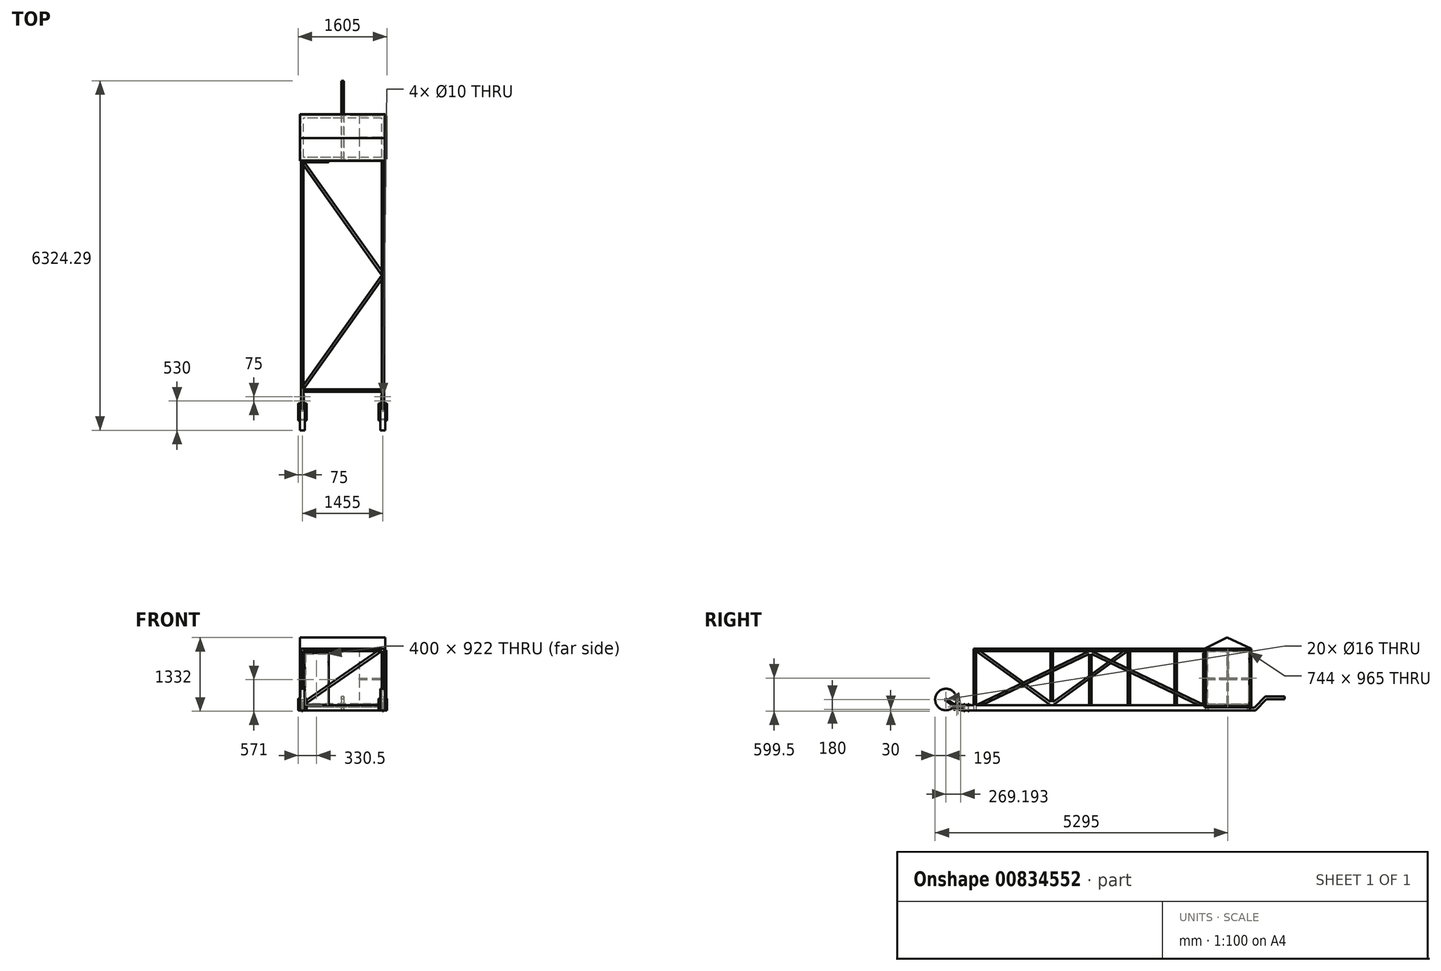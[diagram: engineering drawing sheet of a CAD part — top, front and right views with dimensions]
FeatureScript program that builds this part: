
annotation { "Feature Type Name" : "Feature", "Feature Type Description" : "" }
export const myFeature = defineFeature(function(context is Context, id is Id, definition is map)
    precondition{}
    {
        {
            var Q0;
            Q0=qCreatedBy(makeId("Top.planeOp"),FACE);
            var sketch = newSketch(context, id + "F0", { "sketchPlane" : qUnion([Q0])});
            skLineSegment(sketch, "E0.bottom", {"start": v(750, -2500) * mm, "end": v(-750, -2500) * mm});
            skLineSegment(sketch, "E0.top", {"start": v(750, 2500) * mm, "end": v(-750, 2500) * mm});
            skLineSegment(sketch, "E0.left", {"start": v(750, -2500) * mm, "end": v(750, 2500) * mm});
            skLineSegment(sketch, "E0.right", {"start": v(-750, -2500) * mm, "end": v(-750, 2500) * mm});
            skPoint(sketch, "E0.middle", {"position": v(0, 0) * mm});
            skLineSegment(sketch, "E1.bottom", {"start": v(705, -2455) * mm, "end": v(-705, -2455) * mm});
            skLineSegment(sketch, "E1.top", {"start": v(705, 2455) * mm, "end": v(-705, 2455) * mm});
            skLineSegment(sketch, "E1.left", {"start": v(705, -2455) * mm, "end": v(705, 2455) * mm});
            skLineSegment(sketch, "E1.right", {"start": v(-705, -2455) * mm, "end": v(-705, 2455) * mm});
            skSolve(sketch);
        }
        {
            var Q0;
            Q0 = qSketchRegion(id + "F0", true);
            extrude(context, id + "F1", {"entities" : qUnion([Q0]), "depth" : 95 * mm, "offsetDistance" : 25 * mm});
        }
        {
            var Q0;
            Q0=makeQuery(id+"F1.opExtrude","SWEPT_FACE",FACE,{"disambiguationData":[OSD([sQuery(id+"F0.wireOp",EDGE,"E0.bottom")])]});
            var sketch = newSketch(context, id + "F2", { "sketchPlane" : qUnion([Q0])});
            skLineSegment(sketch, "E2.bottom", {"start": v(750, 95) * mm, "end": v(705, 95) * mm});
            skLineSegment(sketch, "E2.top", {"start": v(750, 0) * mm, "end": v(705, 0) * mm});
            skLineSegment(sketch, "E2.left", {"start": v(750, 95) * mm, "end": v(750, 0) * mm});
            skLineSegment(sketch, "E2.right", {"start": v(705, 95) * mm, "end": v(705, 0) * mm});
            skLineSegment(sketch, "E3.bottom", {"start": v(-750, 95) * mm, "end": v(-705, 95) * mm});
            skLineSegment(sketch, "E3.top", {"start": v(-750, 0) * mm, "end": v(-705, 0) * mm});
            skLineSegment(sketch, "E3.left", {"start": v(-750, 95) * mm, "end": v(-750, 0) * mm});
            skLineSegment(sketch, "E3.right", {"start": v(-705, 95) * mm, "end": v(-705, 0) * mm});
            skSolve(sketch);
        }
        {
            var Q0;
            Q0 = qSketchRegion(id + "F2", true);
            extrude(context, id + "F3", {"entities" : qUnion([Q0]), "operationType" : NewBodyOperationType.ADD, "depth" : 200 * mm, "offsetDistance" : 25 * mm});
        }
        {
            var Q0;
            Q0=makeQuery(id+"F3.opExtrude","SWEPT_FACE",FACE,{"disambiguationData":[OSD([sQuery(id+"F2.wireOp",EDGE,"E2.right")])]});
            var Q1;
            Q1=makeQuery(id+"F3.boolean.opBoolean","MERGE",FACE,{"derivedFrom":[makeQuery(id+"F1.opExtrude","SWEPT_FACE",FACE,{"disambiguationData":[OSD([sQuery(id+"F0.wireOp",EDGE,"E0.left")])]}),makeQuery(id+"F3.opExtrude","SWEPT_FACE",FACE,{"disambiguationData":[OSD([sQuery(id+"F2.wireOp",EDGE,"E2.left")])]})]});
            cPlane(context, id + "F4", {"entities" : qUnion([Q0, Q1]), "cplaneType" : CPlaneType.MID_PLANE, "offset" : 25 * mm, "width" : 150 * mm, "height" : 150 * mm});
        }
        {
            var Q0;
            Q0=qCreatedBy(id+"F4.planeOp",FACE);
            var sketch = newSketch(context, id + "F5", { "sketchPlane" : qUnion([Q0])});
            skCircle(sketch, "E4", {"center": v(3000, 195) * mm, "radius": 195 * mm});
            skLineSegment(sketch, "E5", {"start": v(2248.79, 0) * mm, "end": v(2700, 0) * mm, "construction": true});
            skSolve(sketch);
        }
        {
            var Q0;
            Q0 = qSketchRegion(id + "F5", true);
            extrude(context, id + "F6", {"entities" : qUnion([Q0]), "endBound" : BoundingType.SYMMETRIC, "depth" : 90 * mm, "offsetDistance" : 25 * mm});
        }
        {
            var Q0;
            Q0=makeQuery(id+"F6.opExtrude","CAP_FACE",FACE,{"disambiguationData":[OSD([sQuery(id+"F5.wireOp",EDGE,"E4")])],"isStart":true});
            var sketch = newSketch(context, id + "F7", { "sketchPlane" : qUnion([Q0])});
            skCircle(sketch, "E6", {"center": v(-3000, 195) * mm, "radius": 8 * mm});
            skSolve(sketch);
        }
        {
            var Q0;
            Q0 = qSketchRegion(id + "F7", true);
            extrude(context, id + "F8", {"entities" : qUnion([Q0]), "depth" : 25 * mm, "offsetDistance" : 25 * mm, "hasSecondDirection" : true, "secondDirectionOppositeDirection" : true, "secondDirectionDepth" : (90 + 25) * mm});
        }
        {
            var Q0;
            Q0=makeQuery(id+"F6.opExtrude","CAP_FACE",FACE,{"disambiguationData":[OSD([sQuery(id+"F5.wireOp",EDGE,"E4")])],"isStart":true});
            var sketch = newSketch(context, id + "F9", { "sketchPlane" : qUnion([Q0])});
            skLineSegment(sketch, "E7", {"start": v(-3020.63, 190.75) * mm, "end": v(-2726.68, -5.8) * mm});
            skLineSegment(sketch, "E8", {"start": v(-2726.68, -5.8) * mm, "end": v(-2710, 19.13) * mm});
            skLineSegment(sketch, "E9", {"start": v(-2710, 19.13) * mm, "end": v(-3004.3, 215.93) * mm});
            skLineSegment(sketch, "E10", {"start": v(-3004.3, 215.93) * mm, "end": v(-3020.63, 190.75) * mm});
            skCircle(sketch, "E11.0", {"center": v(-3000, 195) * mm, "radius": 8 * mm});
            skCircle(sketch, "E12", {"center": v(-2730.8, 15) * mm, "radius": 8 * mm});
            skSolve(sketch);
        }
        {
            var Q0;
            Q0 = qSketchRegion(id + "F9", true);
            extrude(context, id + "F10", {"entities" : qUnion([Q0]), "depth" : 30 * mm, "offsetDistance" : 25 * mm});
        }
        {
            var Q0;
            Q0=qCreatedBy(id+"F4.planeOp",FACE);
            var sketch = newSketch(context, id + "F11", { "sketchPlane" : qUnion([Q0])});
            skLineSegment(sketch, "E13.bottom", {"start": v(2700, 95) * mm, "end": v(2555, 95) * mm});
            skLineSegment(sketch, "E13.top", {"start": v(2700, 0) * mm, "end": v(2555, 0) * mm});
            skLineSegment(sketch, "E13.left", {"start": v(2700, 95) * mm, "end": v(2700, 0) * mm});
            skLineSegment(sketch, "E14.bottom", {"start": v(2705, 100) * mm, "end": v(2555, 100) * mm});
            skLineSegment(sketch, "E14.top", {"start": v(2705, -5) * mm, "end": v(2555, -5) * mm});
            skLineSegment(sketch, "E14.left", {"start": v(2705, 100) * mm, "end": v(2705, -5) * mm});
            skLineSegment(sketch, "E14.right", {"start": v(2555, 100) * mm, "end": v(2555, 95) * mm});
            skLineSegment(sketch, "E15.trimOffspring", {"start": v(2555, 0) * mm, "end": v(2555, -5) * mm});
            skSolve(sketch);
        }
        {
            var Q0;
            Q0 = qSketchRegion(id + "F11", true);
            extrude(context, id + "F12", {"entities" : qUnion([Q0]), "endBound" : BoundingType.SYMMETRIC, "oppositeDirection" : true, "depth" : 50 * mm, "offsetDistance" : 25 * mm});
        }
        {
            var Q0;
            Q0=makeQuery(id+"F10.opExtrude","SWEPT_BODY",BODY,{"disambiguationData":[OSD([sQuery(id+"F9.wireOp",EDGE,"E7"),sQuery(id+"F9.wireOp",EDGE,"E8"),sQuery(id+"F9.wireOp",EDGE,"E9"),sQuery(id+"F9.wireOp",EDGE,"E10"),sQuery(id+"F9.wireOp",EDGE,"E11.0"),sQuery(id+"F9.wireOp",EDGE,"E12")])]});
            var Q1;
            Q1=qCreatedBy(id+"F4.planeOp",FACE);
            mirror(context, id + "F13", {"entities" : qUnion([Q0]), "mirrorPlane" : qUnion([Q1])});
        }
        {
            var Q0;
            Q0=makeQuery(id+"F12.opExtrude","CAP_FACE",FACE,{"disambiguationData":[OSD([sQuery(id+"F11.wireOp",EDGE,"E13.bottom"),sQuery(id+"F11.wireOp",EDGE,"E13.top"),sQuery(id+"F11.wireOp",EDGE,"E13.left"),sQuery(id+"F11.wireOp",EDGE,"E14.bottom"),sQuery(id+"F11.wireOp",EDGE,"E14.top"),sQuery(id+"F11.wireOp",EDGE,"E14.left"),sQuery(id+"F11.wireOp",EDGE,"E14.right"),sQuery(id+"F11.wireOp",EDGE,"E15.trimOffspring")])],"isStart":false});
            var sketch = newSketch(context, id + "F14", { "sketchPlane" : qUnion([Q0])});
            skLineSegment(sketch, "E16", {"start": v(-2705, -5) * mm, "end": v(-2735.9, -5) * mm});
            skLineSegment(sketch, "E17", {"start": v(-2802.7, 100) * mm, "end": v(-2705, 100) * mm});
            skLineSegment(sketch, "E18", {"start": v(-2705, 100) * mm, "end": v(-2705, -5) * mm});
            skCircle(sketch, "E19", {"center": v(-2780, 85) * mm, "radius": 8 * mm});
            skLineSegment(sketch, "E20", {"start": v(-2802.7, 100) * mm, "end": v(-2802.7, 78.2) * mm});
            skLineSegment(sketch, "E21", {"start": v(-2802.7, 78.2) * mm, "end": v(-2735.9, -5) * mm});
            skCircle(sketch, "E22.0", {"center": v(-2730.8, 15) * mm, "radius": 8 * mm});
            skSolve(sketch);
        }
        {
            var Q0;
            Q0 = qSketchRegion(id + "F14", true);
            extrude(context, id + "F15", {"entities" : qUnion([Q0]), "oppositeDirection" : true, "depth" : 5 * mm, "offsetDistance" : 25 * mm});
        }
        {
            var Q0;
            Q0=makeQuery(id+"F15.opExtrude","SWEPT_BODY",BODY,{"disambiguationData":[OSD([sQuery(id+"F14.wireOp",EDGE,"E16"),sQuery(id+"F14.wireOp",EDGE,"E17"),sQuery(id+"F14.wireOp",EDGE,"E18"),sQuery(id+"F14.wireOp",EDGE,"E19"),sQuery(id+"F14.wireOp",EDGE,"E20"),sQuery(id+"F14.wireOp",EDGE,"E21"),sQuery(id+"F14.wireOp",EDGE,"E22.0")])]});
            var Q1;
            Q1=qCreatedBy(id+"F4.planeOp",FACE);
            mirror(context, id + "F16", {"entities" : qUnion([Q0]), "mirrorPlane" : qUnion([Q1])});
        }
        {
            var Q0;
            Q0=makeQuery(id+"F10.opExtrude","CAP_FACE",FACE,{"disambiguationData":[OSD([sQuery(id+"F9.wireOp",EDGE,"E7"),sQuery(id+"F9.wireOp",EDGE,"E8"),sQuery(id+"F9.wireOp",EDGE,"E9"),sQuery(id+"F9.wireOp",EDGE,"E10"),sQuery(id+"F9.wireOp",EDGE,"E11.0"),sQuery(id+"F9.wireOp",EDGE,"E12")])],"isStart":false});
            var sketch = newSketch(context, id + "F17", { "sketchPlane" : qUnion([Q0])});
            skCircle(sketch, "E23", {"center": v(-2801.93, 62.56) * mm, "radius": 8 * mm});
            skLineSegment(sketch, "E24", {"start": v(-2146.6, -375.64) * mm, "end": v(-2801.93, 62.56) * mm, "construction": true});
            skLineSegment(sketch, "E25", {"start": v(-2801.93, 62.56) * mm, "end": v(-2730.8, 15) * mm, "construction": true});
            skLineSegment(sketch, "E26", {"start": v(-2730.8, 15) * mm, "end": v(-2780, 85) * mm, "construction": true});
            skCircle(sketch, "E27.0", {"center": v(-2780, 85) * mm, "radius": 8 * mm, "construction": true});
            skSolve(sketch);
        }
        {
            var Q0;
            Q0 = qSketchRegion(id + "F17", true);
            extrude(context, id + "F18", {"entities" : qUnion([Q0]), "operationType" : NewBodyOperationType.REMOVE, "endBound" : BoundingType.THROUGH_ALL, "oppositeDirection" : true, "depth" : 25 * mm, "offsetDistance" : 25 * mm});
        }
        {
            var Q0;
            Q0=makeQuery(id+"F10.opExtrude","CAP_FACE",FACE,{"disambiguationData":[OSD([sQuery(id+"F9.wireOp",EDGE,"E7"),sQuery(id+"F9.wireOp",EDGE,"E8"),sQuery(id+"F9.wireOp",EDGE,"E9"),sQuery(id+"F9.wireOp",EDGE,"E10"),sQuery(id+"F9.wireOp",EDGE,"E11.0"),sQuery(id+"F9.wireOp",EDGE,"E12")])],"isStart":false});
            var sketch = newSketch(context, id + "F19", { "sketchPlane" : qUnion([Q0])});
            skCircle(sketch, "E28.0", {"center": v(-2801.93, 62.56) * mm, "radius": 8 * mm});
            skSolve(sketch);
        }
        {
            var Q0;
            Q0 = qSketchRegion(id + "F19", true);
            var Q1;
            Q1=makeQuery(id+"F13.opPattern","COPY",FACE,{"derivedFrom":makeQuery(id+"F10.opExtrude","CAP_FACE",FACE,{"disambiguationData":[OSD([sQuery(id+"F9.wireOp",EDGE,"E7"),sQuery(id+"F9.wireOp",EDGE,"E8"),sQuery(id+"F9.wireOp",EDGE,"E9"),sQuery(id+"F9.wireOp",EDGE,"E10"),sQuery(id+"F9.wireOp",EDGE,"E11.0"),sQuery(id+"F9.wireOp",EDGE,"E12")])],"isStart":false}),"instanceName":"1"});
            extrude(context, id + "F20", {"entities" : qUnion([Q0]), "endBound" : BoundingType.UP_TO_SURFACE, "oppositeDirection" : true, "depth" : 25 * mm, "endBoundEntityFace" : qUnion([Q1]), "offsetDistance" : 25 * mm});
        }
        {
            var Q0;
            Q0=makeQuery(id+"F16.opPattern","COPY",FACE,{"derivedFrom":makeQuery(id+"F15.opExtrude","CAP_FACE",FACE,{"disambiguationData":[OSD([sQuery(id+"F14.wireOp",EDGE,"E16"),sQuery(id+"F14.wireOp",EDGE,"E17"),sQuery(id+"F14.wireOp",EDGE,"E18"),sQuery(id+"F14.wireOp",EDGE,"E19"),sQuery(id+"F14.wireOp",EDGE,"E20"),sQuery(id+"F14.wireOp",EDGE,"E21"),sQuery(id+"F14.wireOp",EDGE,"E22.0")])],"isStart":true}),"instanceName":"1"});
            var sketch = newSketch(context, id + "F21", { "sketchPlane" : qUnion([Q0])});
            skCircle(sketch, "E29.0", {"center": v(2780, 85) * mm, "radius": 8 * mm});
            skSolve(sketch);
        }
        {
            var Q0;
            Q0 = qSketchRegion(id + "F21", true);
            var Q1;
            Q1=makeQuery(id+"F15.opExtrude","CAP_FACE",FACE,{"disambiguationData":[OSD([sQuery(id+"F14.wireOp",EDGE,"E16"),sQuery(id+"F14.wireOp",EDGE,"E17"),sQuery(id+"F14.wireOp",EDGE,"E18"),sQuery(id+"F14.wireOp",EDGE,"E19"),sQuery(id+"F14.wireOp",EDGE,"E20"),sQuery(id+"F14.wireOp",EDGE,"E21"),sQuery(id+"F14.wireOp",EDGE,"E22.0")])],"isStart":true});
            extrude(context, id + "F22", {"entities" : qUnion([Q0]), "endBound" : BoundingType.UP_TO_SURFACE, "oppositeDirection" : true, "depth" : 25 * mm, "endBoundEntityFace" : qUnion([Q1]), "offsetDistance" : 25 * mm});
        }
        {
            var Q0;
            Q0=makeQuery(id+"F10.opExtrude","CAP_FACE",FACE,{"disambiguationData":[OSD([sQuery(id+"F9.wireOp",EDGE,"E7"),sQuery(id+"F9.wireOp",EDGE,"E8"),sQuery(id+"F9.wireOp",EDGE,"E9"),sQuery(id+"F9.wireOp",EDGE,"E10"),sQuery(id+"F9.wireOp",EDGE,"E11.0"),sQuery(id+"F9.wireOp",EDGE,"E12")])],"isStart":false});
            var sketch = newSketch(context, id + "F23", { "sketchPlane" : qUnion([Q0])});
            skCircle(sketch, "E30.0", {"center": v(-2730.8, 15) * mm, "radius": 8 * mm});
            skSolve(sketch);
        }
        {
            var Q0;
            Q0 = qSketchRegion(id + "F23", true);
            var Q1;
            Q1=makeQuery(id+"F13.opPattern","COPY",FACE,{"derivedFrom":makeQuery(id+"F10.opExtrude","CAP_FACE",FACE,{"disambiguationData":[OSD([sQuery(id+"F9.wireOp",EDGE,"E7"),sQuery(id+"F9.wireOp",EDGE,"E8"),sQuery(id+"F9.wireOp",EDGE,"E9"),sQuery(id+"F9.wireOp",EDGE,"E10"),sQuery(id+"F9.wireOp",EDGE,"E11.0"),sQuery(id+"F9.wireOp",EDGE,"E12")])],"isStart":false}),"instanceName":"1"});
            extrude(context, id + "F24", {"entities" : qUnion([Q0]), "endBound" : BoundingType.UP_TO_SURFACE, "oppositeDirection" : true, "depth" : 25 * mm, "endBoundEntityFace" : qUnion([Q1]), "offsetDistance" : 25 * mm});
        }
        {
            var Q0;
            Q0=makeQuery(id+"F15.opExtrude","SWEPT_EDGE",EDGE,{"disambiguationData":[OSD([sQuery(id+"F14.wireOp",EDGE,"E17"),sQuery(id+"F14.wireOp",EDGE,"E20")])]});
            cPlane(context, id + "F25", {"entities" : qUnion([Q0]), "cplaneType" : CPlaneType.LINE_ANGLE, "offset" : 25 * mm, "angle" : 47 * degree, "width" : 150 * mm, "height" : 150 * mm});
        }
        {
            var Q0;
            Q0=qCreatedBy(id+"F25.planeOp",FACE);
            var sketch = newSketch(context, id + "F26", { "sketchPlane" : qUnion([Q0])});
            skCircle(sketch, "E31", {"center": v(727.5, -2091.13) * mm, "radius": 6 * mm});
            skLineSegment(sketch, "E32", {"start": v(1068.27, -2099.13) * mm, "end": v(887.35, -2099.13) * mm, "construction": true});
            skLineSegment(sketch, "E33", {"start": v(882.86, -2083.13) * mm, "end": v(1061.54, -2083.13) * mm, "construction": true});
            skLineSegment(sketch, "E34", {"start": v(727.5, -2091.13) * mm, "end": v(883.31, -2091.13) * mm, "construction": true});
            skLineSegment(sketch, "E35", {"start": v(727.5, -2091.13) * mm, "end": v(727.5, -2020.53) * mm, "construction": true});
            skSolve(sketch);
        }
        {
            var Q0;
            Q0 = qSketchRegion(id + "F26", true);
            extrude(context, id + "F27", {"entities" : qUnion([Q0]), "depth" : 50 * mm, "offsetDistance" : 25 * mm, "hasSecondDirection" : true, "secondDirectionOppositeDirection" : true, "secondDirectionDepth" : 100 * mm});
        }
        {
            var Q0;
            Q0=makeQuery(id+"F27.opExtrude","CAP_FACE",FACE,{"disambiguationData":[OSD([sQuery(id+"F26.wireOp",EDGE,"E31")])],"isStart":false});
            var sketch = newSketch(context, id + "F28", { "sketchPlane" : qUnion([Q0])});
            skCircle(sketch, "E36.cCircle", {"center": v(727.5, -2091.13) * mm, "radius": 9.5 * mm, "construction": true});
            skLineSegment(sketch, "E36.0", {"start": v(722.02, -2081.63) * mm, "end": v(732.98, -2081.63) * mm});
            skLineSegment(sketch, "E36.1", {"start": v(732.98, -2081.63) * mm, "end": v(738.47, -2091.13) * mm});
            skLineSegment(sketch, "E36.2", {"start": v(738.47, -2091.13) * mm, "end": v(732.98, -2100.63) * mm});
            skLineSegment(sketch, "E36.3", {"start": v(732.98, -2100.63) * mm, "end": v(722.02, -2100.63) * mm});
            skLineSegment(sketch, "E36.4", {"start": v(722.02, -2100.63) * mm, "end": v(716.53, -2091.13) * mm});
            skLineSegment(sketch, "E36.5", {"start": v(716.53, -2091.13) * mm, "end": v(722.02, -2081.63) * mm});
            skPoint(sketch, "E36.0.midPoint", {"position": v(727.5, -2081.63) * mm});
            skSolve(sketch);
        }
        {
            var Q0;
            Q0 = qSketchRegion(id + "F28", true);
            extrude(context, id + "F29", {"entities" : qUnion([Q0]), "operationType" : NewBodyOperationType.ADD, "depth" : 12 * mm, "offsetDistance" : 25 * mm});
        }
        {
            var Q0;
            Q0=makeQuery(id+"F27.opExtrude","SWEPT_BODY",BODY,{"disambiguationData":[OSD([sQuery(id+"F26.wireOp",EDGE,"E31")])]});
            var Q1;
            Q1=makeQuery(id+"F20.opExtrude","SWEPT_BODY",BODY,{"disambiguationData":[OSD([sQuery(id+"F19.wireOp",EDGE,"E28.0")])]});
            var Q2;
            Q2=makeQuery(id+"F22.opExtrude","SWEPT_BODY",BODY,{"disambiguationData":[OSD([sQuery(id+"F21.wireOp",EDGE,"E29.0")])]});
            booleanBodies(context, id + "F30", {"operationType" : BooleanOperationType.SUBTRACTION, "tools" : qUnion([Q0]), "targets" : qUnion([Q1, Q2]), "keepTools" : true});
        }
        {
            var Q0;
            Q0=makeQuery(id+"F12.opExtrude","SWEPT_FACE",FACE,{"disambiguationData":[OSD([sQuery(id+"F11.wireOp",EDGE,"E14.bottom")])]});
            var sketch = newSketch(context, id + "F31", { "sketchPlane" : qUnion([Q0])});
            skCircle(sketch, "E37", {"center": v(727.5, -2665) * mm, "radius": 5 * mm});
            skCircle(sketch, "E38", {"center": v(727.5, -2590) * mm, "radius": 5 * mm});
            skLineSegment(sketch, "E39", {"start": v(727.5, -2665) * mm, "end": v(727.5, -2590) * mm, "construction": true});
            skSolve(sketch);
        }
        {
            var Q0;
            Q0 = qSketchRegion(id + "F31", true);
            extrude(context, id + "F32", {"entities" : qUnion([Q0]), "oppositeDirection" : true, "depth" : 115 * mm, "offsetDistance" : 25 * mm});
        }
        {
            var Q0;
            Q0=makeQuery(id+"F12.opExtrude","SWEPT_FACE",FACE,{"disambiguationData":[OSD([sQuery(id+"F11.wireOp",EDGE,"E14.top")])]});
            var sketch = newSketch(context, id + "F33", { "sketchPlane" : qUnion([Q0])});
            skCircle(sketch, "E40.0", {"center": v(727.5, 2665) * mm, "radius": 5 * mm});
            skCircle(sketch, "E41.0", {"center": v(727.5, 2590) * mm, "radius": 5 * mm});
            skCircle(sketch, "E42.cCircle", {"center": v(727.5, 2665) * mm, "radius": 8.5 * mm, "construction": true});
            skLineSegment(sketch, "E42.0", {"start": v(724.08, 2655.8) * mm, "end": v(717.82, 2663.37) * mm});
            skLineSegment(sketch, "E42.1", {"start": v(717.82, 2663.37) * mm, "end": v(721.25, 2672.56) * mm});
            skLineSegment(sketch, "E42.2", {"start": v(721.25, 2672.56) * mm, "end": v(730.92, 2674.2) * mm});
            skLineSegment(sketch, "E42.3", {"start": v(730.92, 2674.2) * mm, "end": v(737.18, 2666.63) * mm});
            skLineSegment(sketch, "E42.4", {"start": v(737.18, 2666.63) * mm, "end": v(733.75, 2657.44) * mm});
            skLineSegment(sketch, "E42.5", {"start": v(733.75, 2657.44) * mm, "end": v(724.08, 2655.8) * mm});
            skPoint(sketch, "E42.0.midPoint", {"position": v(720.95, 2659.58) * mm});
            skCircle(sketch, "E43.cCircle", {"center": v(727.5, 2590) * mm, "radius": 8.5 * mm, "construction": true});
            skLineSegment(sketch, "E43.0", {"start": v(720.8, 2582.83) * mm, "end": v(717.94, 2592.22) * mm});
            skLineSegment(sketch, "E43.1", {"start": v(717.94, 2592.22) * mm, "end": v(724.65, 2599.4) * mm});
            skLineSegment(sketch, "E43.2", {"start": v(724.65, 2599.4) * mm, "end": v(734.2, 2597.17) * mm});
            skLineSegment(sketch, "E43.3", {"start": v(734.2, 2597.17) * mm, "end": v(737.06, 2587.78) * mm});
            skLineSegment(sketch, "E43.4", {"start": v(737.06, 2587.78) * mm, "end": v(730.35, 2580.6) * mm});
            skLineSegment(sketch, "E43.5", {"start": v(730.35, 2580.6) * mm, "end": v(720.8, 2582.83) * mm});
            skPoint(sketch, "E43.0.midPoint", {"position": v(719.37, 2587.53) * mm});
            skSolve(sketch);
        }
        {
            var Q0;
            Q0 = qSketchRegion(id + "F33", true);
            extrude(context, id + "F34", {"entities" : qUnion([Q0]), "depth" : 10 * mm, "offsetDistance" : 25 * mm});
        }
        {
            var Q0;
            Q0=makeQuery(id+"F12.opExtrude","SWEPT_FACE",FACE,{"disambiguationData":[OSD([sQuery(id+"F11.wireOp",EDGE,"E14.bottom")])]});
            var sketch = newSketch(context, id + "F35", { "sketchPlane" : qUnion([Q0])});
            skCircle(sketch, "E44.cCircle", {"center": v(727.5, -2665) * mm, "radius": 8.5 * mm, "construction": true});
            skLineSegment(sketch, "E44.0", {"start": v(730.24, -2655.58) * mm, "end": v(737.03, -2662.66) * mm});
            skLineSegment(sketch, "E44.1", {"start": v(737.03, -2662.66) * mm, "end": v(734.3, -2672.09) * mm});
            skLineSegment(sketch, "E44.2", {"start": v(734.3, -2672.09) * mm, "end": v(724.76, -2674.42) * mm});
            skLineSegment(sketch, "E44.3", {"start": v(724.76, -2674.42) * mm, "end": v(717.97, -2667.34) * mm});
            skLineSegment(sketch, "E44.4", {"start": v(717.97, -2667.34) * mm, "end": v(720.7, -2657.91) * mm});
            skLineSegment(sketch, "E44.5", {"start": v(720.7, -2657.91) * mm, "end": v(730.24, -2655.58) * mm});
            skPoint(sketch, "E44.0.midPoint", {"position": v(733.64, -2659.12) * mm});
            skCircle(sketch, "E45.cCircle", {"center": v(727.5, -2590) * mm, "radius": 8.5 * mm, "construction": true});
            skLineSegment(sketch, "E45.0", {"start": v(732.8, -2581.73) * mm, "end": v(737.3, -2590.45) * mm});
            skLineSegment(sketch, "E45.1", {"start": v(737.3, -2590.45) * mm, "end": v(732.01, -2598.72) * mm});
            skLineSegment(sketch, "E45.2", {"start": v(732.01, -2598.72) * mm, "end": v(722.2, -2598.27) * mm});
            skLineSegment(sketch, "E45.3", {"start": v(722.2, -2598.27) * mm, "end": v(717.7, -2589.55) * mm});
            skLineSegment(sketch, "E45.4", {"start": v(717.7, -2589.55) * mm, "end": v(722.99, -2581.28) * mm});
            skLineSegment(sketch, "E45.5", {"start": v(722.99, -2581.28) * mm, "end": v(732.8, -2581.73) * mm});
            skPoint(sketch, "E45.0.midPoint", {"position": v(735.05, -2586.1) * mm});
            skSolve(sketch);
        }
        {
            var Q0;
            Q0 = qSketchRegion(id + "F35", true);
            extrude(context, id + "F36", {"entities" : qUnion([Q0]), "operationType" : NewBodyOperationType.ADD, "depth" : 10 * mm, "offsetDistance" : 25 * mm});
        }
        {
            var Q0;
            Q0=makeQuery(id+"F6.opExtrude","SWEPT_BODY",BODY,{"disambiguationData":[OSD([sQuery(id+"F5.wireOp",EDGE,"E4")])]});
            var Q1;
            Q1=makeQuery(id+"F8.opExtrude","SWEPT_BODY",BODY,{"disambiguationData":[OSD([sQuery(id+"F7.wireOp",EDGE,"E6")])]});
            var Q2;
            Q2=makeQuery(id+"F10.opExtrude","SWEPT_BODY",BODY,{"disambiguationData":[OSD([sQuery(id+"F9.wireOp",EDGE,"E7"),sQuery(id+"F9.wireOp",EDGE,"E8"),sQuery(id+"F9.wireOp",EDGE,"E9"),sQuery(id+"F9.wireOp",EDGE,"E10"),sQuery(id+"F9.wireOp",EDGE,"E11.0"),sQuery(id+"F9.wireOp",EDGE,"E12")])]});
            var Q3;
            Q3=makeQuery(id+"F12.opExtrude","SWEPT_BODY",BODY,{"disambiguationData":[OSD([sQuery(id+"F11.wireOp",EDGE,"E13.bottom"),sQuery(id+"F11.wireOp",EDGE,"E13.top"),sQuery(id+"F11.wireOp",EDGE,"E13.left"),sQuery(id+"F11.wireOp",EDGE,"E14.bottom"),sQuery(id+"F11.wireOp",EDGE,"E14.top"),sQuery(id+"F11.wireOp",EDGE,"E14.left"),sQuery(id+"F11.wireOp",EDGE,"E14.right"),sQuery(id+"F11.wireOp",EDGE,"E15.trimOffspring")])]});
            var Q4;
            Q4=makeQuery(id+"F13.opPattern","COPY",BODY,{"derivedFrom":makeQuery(id+"F10.opExtrude","SWEPT_BODY",BODY,{"disambiguationData":[OSD([sQuery(id+"F9.wireOp",EDGE,"E7"),sQuery(id+"F9.wireOp",EDGE,"E8"),sQuery(id+"F9.wireOp",EDGE,"E9"),sQuery(id+"F9.wireOp",EDGE,"E10"),sQuery(id+"F9.wireOp",EDGE,"E11.0"),sQuery(id+"F9.wireOp",EDGE,"E12")])]}),"instanceName":"1"});
            var Q5;
            Q5=makeQuery(id+"F15.opExtrude","SWEPT_BODY",BODY,{"disambiguationData":[OSD([sQuery(id+"F14.wireOp",EDGE,"E16"),sQuery(id+"F14.wireOp",EDGE,"E17"),sQuery(id+"F14.wireOp",EDGE,"E18"),sQuery(id+"F14.wireOp",EDGE,"E19"),sQuery(id+"F14.wireOp",EDGE,"E20"),sQuery(id+"F14.wireOp",EDGE,"E21"),sQuery(id+"F14.wireOp",EDGE,"E22.0")])]});
            var Q6;
            Q6=makeQuery(id+"F16.opPattern","COPY",BODY,{"derivedFrom":makeQuery(id+"F15.opExtrude","SWEPT_BODY",BODY,{"disambiguationData":[OSD([sQuery(id+"F14.wireOp",EDGE,"E16"),sQuery(id+"F14.wireOp",EDGE,"E17"),sQuery(id+"F14.wireOp",EDGE,"E18"),sQuery(id+"F14.wireOp",EDGE,"E19"),sQuery(id+"F14.wireOp",EDGE,"E20"),sQuery(id+"F14.wireOp",EDGE,"E21"),sQuery(id+"F14.wireOp",EDGE,"E22.0")])]}),"instanceName":"1"});
            var Q7;
            Q7=makeQuery(id+"F20.opExtrude","SWEPT_BODY",BODY,{"disambiguationData":[OSD([sQuery(id+"F19.wireOp",EDGE,"E28.0")])]});
            var Q8;
            Q8=makeQuery(id+"F22.opExtrude","SWEPT_BODY",BODY,{"disambiguationData":[OSD([sQuery(id+"F21.wireOp",EDGE,"E29.0")])]});
            var Q9;
            Q9=makeQuery(id+"F24.opExtrude","SWEPT_BODY",BODY,{"disambiguationData":[OSD([sQuery(id+"F23.wireOp",EDGE,"E30.0")])]});
            var Q10;
            Q10=makeQuery(id+"F27.opExtrude","SWEPT_BODY",BODY,{"disambiguationData":[OSD([sQuery(id+"F26.wireOp",EDGE,"E31")])]});
            var Q11;
            Q11=makeQuery(id+"F32.opExtrude","SWEPT_BODY",BODY,{"disambiguationData":[OSD([sQuery(id+"F31.wireOp",EDGE,"E37")])]});
            var Q12;
            Q12=makeQuery(id+"F32.opExtrude","SWEPT_BODY",BODY,{"disambiguationData":[OSD([sQuery(id+"F31.wireOp",EDGE,"E38")])]});
            var Q13;
            Q13=makeQuery(id+"F34.opExtrude","SWEPT_BODY",BODY,{"disambiguationData":[OSD([sQuery(id+"F33.wireOp",EDGE,"E40.0"),sQuery(id+"F33.wireOp",EDGE,"E42.0"),sQuery(id+"F33.wireOp",EDGE,"E42.1"),sQuery(id+"F33.wireOp",EDGE,"E42.2"),sQuery(id+"F33.wireOp",EDGE,"E42.3"),sQuery(id+"F33.wireOp",EDGE,"E42.4"),sQuery(id+"F33.wireOp",EDGE,"E42.5")])]});
            var Q14;
            Q14=makeQuery(id+"F34.opExtrude","SWEPT_BODY",BODY,{"disambiguationData":[OSD([sQuery(id+"F33.wireOp",EDGE,"E41.0"),sQuery(id+"F33.wireOp",EDGE,"E43.0"),sQuery(id+"F33.wireOp",EDGE,"E43.1"),sQuery(id+"F33.wireOp",EDGE,"E43.2"),sQuery(id+"F33.wireOp",EDGE,"E43.3"),sQuery(id+"F33.wireOp",EDGE,"E43.4"),sQuery(id+"F33.wireOp",EDGE,"E43.5")])]});
            var Q15;
            Q15=qCreatedBy(makeId("Right.planeOp"),FACE);
            mirror(context, id + "F37", {"entities" : qUnion([Q0, Q1, Q2, Q3, Q4, Q5, Q6, Q7, Q8, Q9, Q10, Q11, Q12, Q13, Q14]), "mirrorPlane" : qUnion([Q15])});
        }
        {
            var Q0;
            Q0=makeQuery(id+"F1.opExtrude","SWEPT_FACE",FACE,{"disambiguationData":[OSD([sQuery(id+"F0.wireOp",EDGE,"E1.right")])]});
            var sketch = newSketch(context, id + "F38", { "sketchPlane" : qUnion([Q0])});
            skLineSegment(sketch, "E46.bottom", {"start": v(1700, 95) * mm, "end": v(1745, 95) * mm});
            skLineSegment(sketch, "E46.top", {"start": v(1700, 0) * mm, "end": v(1745, 0) * mm});
            skLineSegment(sketch, "E46.left", {"start": v(1700, 95) * mm, "end": v(1700, 0) * mm});
            skLineSegment(sketch, "E46.right", {"start": v(1745, 95) * mm, "end": v(1745, 0) * mm});
            skSolve(sketch);
        }
        {
            var Q0;
            Q0 = qSketchRegion(id + "F38", true);
            extrude(context, id + "F39", {"entities" : qUnion([Q0]), "operationType" : NewBodyOperationType.ADD, "endBound" : BoundingType.UP_TO_NEXT, "depth" : 25 * mm, "offsetDistance" : 25 * mm});
        }
        {
            var Q0;
            Q0=makeQuery(id+"F39.boolean.opBoolean","MERGE",FACE,{"derivedFrom":[makeQuery(id+"F3.boolean.opBoolean","MERGE",FACE,{"derivedFrom":[makeQuery(id+"F1.opExtrude","CAP_FACE",FACE,{"disambiguationData":[OSD([sQuery(id+"F0.wireOp",EDGE,"E0.bottom"),sQuery(id+"F0.wireOp",EDGE,"E0.top"),sQuery(id+"F0.wireOp",EDGE,"E0.left"),sQuery(id+"F0.wireOp",EDGE,"E0.right"),sQuery(id+"F0.wireOp",EDGE,"E1.bottom"),sQuery(id+"F0.wireOp",EDGE,"E1.top"),sQuery(id+"F0.wireOp",EDGE,"E1.left"),sQuery(id+"F0.wireOp",EDGE,"E1.right")])],"isStart":false}),makeQuery(id+"F3.opExtrude","SWEPT_FACE",FACE,{"disambiguationData":[OSD([sQuery(id+"F2.wireOp",EDGE,"E2.bottom")])]}),makeQuery(id+"F3.opExtrude","SWEPT_FACE",FACE,{"disambiguationData":[OSD([sQuery(id+"F2.wireOp",EDGE,"E3.bottom")])]})]}),makeQuery(id+"F39.opExtrude","SWEPT_FACE",FACE,{"disambiguationData":[OSD([sQuery(id+"F38.wireOp",EDGE,"E46.bottom")])]})]});
            var sketch = newSketch(context, id + "F40", { "sketchPlane" : qUnion([Q0])});
            skLineSegment(sketch, "E47.bottom", {"start": v(-750, 1700) * mm, "end": v(750, 1700) * mm});
            skLineSegment(sketch, "E47.top", {"start": v(-750, 2500) * mm, "end": v(750, 2500) * mm});
            skLineSegment(sketch, "E47.left", {"start": v(-750, 1700) * mm, "end": v(-750, 2500) * mm});
            skLineSegment(sketch, "E47.right", {"start": v(750, 1700) * mm, "end": v(750, 2500) * mm});
            skSolve(sketch);
        }
        {
            var Q0;
            Q0 = qSketchRegion(id + "F40", true);
            extrude(context, id + "F41", {"entities" : qUnion([Q0]), "depth" : 22 * mm, "offsetDistance" : 25 * mm});
        }
        {
            var Q0;
            Q0=makeQuery(id+"F41.opExtrude","CAP_FACE",FACE,{"disambiguationData":[OSD([sQuery(id+"F40.wireOp",EDGE,"E47.bottom"),sQuery(id+"F40.wireOp",EDGE,"E47.top"),sQuery(id+"F40.wireOp",EDGE,"E47.left"),sQuery(id+"F40.wireOp",EDGE,"E47.right")])],"isStart":false});
            var sketch = newSketch(context, id + "F42", { "sketchPlane" : qUnion([Q0])});
            skLineSegment(sketch, "E48.bottom", {"start": v(750, 1700) * mm, "end": v(-750, 1700) * mm});
            skLineSegment(sketch, "E48.top", {"start": v(750, 2500) * mm, "end": v(-750, 2500) * mm});
            skLineSegment(sketch, "E48.left", {"start": v(750, 1700) * mm, "end": v(750, 2500) * mm});
            skLineSegment(sketch, "E48.right", {"start": v(-750, 1700) * mm, "end": v(-750, 2500) * mm});
            skLineSegment(sketch, "E49.bottom", {"start": v(772, 1678) * mm, "end": v(-772, 1678) * mm});
            skLineSegment(sketch, "E49.top", {"start": v(772, 2522) * mm, "end": v(-772, 2522) * mm});
            skLineSegment(sketch, "E49.left", {"start": v(772, 1678) * mm, "end": v(772, 2522) * mm});
            skLineSegment(sketch, "E49.right", {"start": v(-772, 1678) * mm, "end": v(-772, 2522) * mm});
            skSolve(sketch);
        }
        {
            var Q0;
            Q0 = qSketchRegion(id + "F42", true);
            extrude(context, id + "F43", {"entities" : qUnion([Q0]), "oppositeDirection" : true, "depth" : 65 * mm, "offsetDistance" : 25 * mm, "hasSecondDirection" : true, "secondDirectionOppositeDirection" : false, "secondDirectionDepth" : 1000 * mm});
        }
        {
            var Q0;
            Q0=qCreatedBy(makeId("Right.planeOp"),FACE);
            var sketch = newSketch(context, id + "F44", { "sketchPlane" : qUnion([Q0])});
            skLineSegment(sketch, "E50", {"start": v(1700, 0) * mm, "end": v(2600, 0) * mm});
            skLineSegment(sketch, "E51", {"start": v(2600, 0) * mm, "end": v(2800, 200) * mm});
            skLineSegment(sketch, "E52", {"start": v(2800, 200) * mm, "end": v(3129.29, 200) * mm});
            skLineSegment(sketch, "E53", {"start": v(3129.29, 200) * mm, "end": v(3129.29, 250) * mm});
            skLineSegment(sketch, "E54", {"start": v(3129.29, 250) * mm, "end": v(2779.29, 250) * mm});
            skLineSegment(sketch, "E55", {"start": v(2779.29, 250) * mm, "end": v(2579.29, 50) * mm});
            skLineSegment(sketch, "E56", {"start": v(2579.29, 50) * mm, "end": v(1700, 50) * mm});
            skLineSegment(sketch, "E57", {"start": v(1700, 50) * mm, "end": v(1700, 0) * mm});
            skLineSegment(sketch, "E58.0", {"start": v(1700, 95) * mm, "end": v(1700, 0) * mm, "construction": true});
            skSolve(sketch);
        }
        {
            var Q0;
            Q0 = qSketchRegion(id + "F44", true);
            extrude(context, id + "F45", {"entities" : qUnion([Q0]), "endBound" : BoundingType.SYMMETRIC, "depth" : 50 * mm, "offsetDistance" : 25 * mm});
        }
        {
            var Q0;
            Q0=makeQuery(id+"F45.opExtrude","SWEPT_BODY",BODY,{"disambiguationData":[OSD([sQuery(id+"F44.wireOp",EDGE,"E50"),sQuery(id+"F44.wireOp",EDGE,"E51"),sQuery(id+"F44.wireOp",EDGE,"E52"),sQuery(id+"F44.wireOp",EDGE,"E53"),sQuery(id+"F44.wireOp",EDGE,"E54"),sQuery(id+"F44.wireOp",EDGE,"E55"),sQuery(id+"F44.wireOp",EDGE,"E56"),sQuery(id+"F44.wireOp",EDGE,"E57")])]});
            var Q1;
            Q1=makeQuery(id+"F1.opExtrude","SWEPT_BODY",BODY,{"disambiguationData":[OSD([sQuery(id+"F0.wireOp",EDGE,"E0.bottom"),sQuery(id+"F0.wireOp",EDGE,"E0.top"),sQuery(id+"F0.wireOp",EDGE,"E0.left"),sQuery(id+"F0.wireOp",EDGE,"E0.right"),sQuery(id+"F0.wireOp",EDGE,"E1.bottom"),sQuery(id+"F0.wireOp",EDGE,"E1.top"),sQuery(id+"F0.wireOp",EDGE,"E1.left"),sQuery(id+"F0.wireOp",EDGE,"E1.right")])]});
            booleanBodies(context, id + "F46", {"operationType" : BooleanOperationType.SUBTRACTION, "tools" : qUnion([Q0]), "targets" : qUnion([Q1]), "keepTools" : true});
        }
        {
            var Q0;
            Q0=makeQuery(id+"F39.boolean.opBoolean","MERGE",FACE,{"derivedFrom":[makeQuery(id+"F3.boolean.opBoolean","MERGE",FACE,{"derivedFrom":[makeQuery(id+"F1.opExtrude","CAP_FACE",FACE,{"disambiguationData":[OSD([sQuery(id+"F0.wireOp",EDGE,"E0.bottom"),sQuery(id+"F0.wireOp",EDGE,"E0.top"),sQuery(id+"F0.wireOp",EDGE,"E0.left"),sQuery(id+"F0.wireOp",EDGE,"E0.right"),sQuery(id+"F0.wireOp",EDGE,"E1.bottom"),sQuery(id+"F0.wireOp",EDGE,"E1.top"),sQuery(id+"F0.wireOp",EDGE,"E1.left"),sQuery(id+"F0.wireOp",EDGE,"E1.right")])],"isStart":false}),makeQuery(id+"F3.opExtrude","SWEPT_FACE",FACE,{"disambiguationData":[OSD([sQuery(id+"F2.wireOp",EDGE,"E2.bottom")])]}),makeQuery(id+"F3.opExtrude","SWEPT_FACE",FACE,{"disambiguationData":[OSD([sQuery(id+"F2.wireOp",EDGE,"E3.bottom")])]})]}),makeQuery(id+"F39.opExtrude","SWEPT_FACE",FACE,{"disambiguationData":[OSD([sQuery(id+"F38.wireOp",EDGE,"E46.bottom")])]})]});
            var sketch = newSketch(context, id + "F47", { "sketchPlane" : qUnion([Q0])});
            skLineSegment(sketch, "E59.bottom", {"start": v(-705, -2455) * mm, "end": v(-750, -2455) * mm});
            skLineSegment(sketch, "E59.top", {"start": v(-705, -2500) * mm, "end": v(-750, -2500) * mm});
            skLineSegment(sketch, "E59.left", {"start": v(-705, -2455) * mm, "end": v(-705, -2500) * mm});
            skLineSegment(sketch, "E59.right", {"start": v(-750, -2455) * mm, "end": v(-750, -2500) * mm});
            skLineSegment(sketch, "E60.bottom", {"start": v(705, -2455) * mm, "end": v(750, -2455) * mm});
            skLineSegment(sketch, "E60.top", {"start": v(705, -2500) * mm, "end": v(750, -2500) * mm});
            skLineSegment(sketch, "E60.left", {"start": v(705, -2455) * mm, "end": v(705, -2500) * mm});
            skLineSegment(sketch, "E60.right", {"start": v(750, -2455) * mm, "end": v(750, -2500) * mm});
            skSolve(sketch);
        }
        {
            var Q0;
            Q0 = qSketchRegion(id + "F47", true);
            var Q1;
            Q1=makeQuery(id+"F43.opExtrude","CAP_FACE",FACE,{"disambiguationData":[OSD([sQuery(id+"F42.wireOp",EDGE,"E48.bottom"),sQuery(id+"F42.wireOp",EDGE,"E48.top"),sQuery(id+"F42.wireOp",EDGE,"E48.left"),sQuery(id+"F42.wireOp",EDGE,"E48.right"),sQuery(id+"F42.wireOp",EDGE,"E49.bottom"),sQuery(id+"F42.wireOp",EDGE,"E49.top"),sQuery(id+"F42.wireOp",EDGE,"E49.left"),sQuery(id+"F42.wireOp",EDGE,"E49.right")])],"isStart":true});
            extrude(context, id + "F48", {"entities" : qUnion([Q0]), "operationType" : NewBodyOperationType.ADD, "endBound" : BoundingType.UP_TO_SURFACE, "depth" : 25 * mm, "endBoundEntityFace" : qUnion([Q1]), "offsetDistance" : 25 * mm});
        }
        {
            var Q0;
            Q0=makeQuery(id+"F43.opExtrude","SWEPT_FACE",FACE,{"disambiguationData":[OSD([sQuery(id+"F42.wireOp",EDGE,"E49.bottom")])]});
            var sketch = newSketch(context, id + "F49", { "sketchPlane" : qUnion([Q0])});
            skLineSegment(sketch, "E61.bottom", {"start": v(-672, 1017) * mm, "end": v(-272, 1017) * mm});
            skLineSegment(sketch, "E61.top", {"start": v(-672, 95) * mm, "end": v(-272, 95) * mm});
            skLineSegment(sketch, "E61.left", {"start": v(-672, 1017) * mm, "end": v(-672, 95) * mm});
            skLineSegment(sketch, "E61.right", {"start": v(-272, 1017) * mm, "end": v(-272, 95) * mm});
            skSolve(sketch);
        }
        {
            var Q0;
            Q0 = qSketchRegion(id + "F49", true);
            extrude(context, id + "F50", {"entities" : qUnion([Q0]), "operationType" : NewBodyOperationType.REMOVE, "oppositeDirection" : true, "depth" : 25 * mm, "offsetDistance" : 25 * mm});
        }
        {
            var Q0;
            Q0=makeQuery(id+"F48.opExtrude","SWEPT_FACE",FACE,{"disambiguationData":[OSD([sQuery(id+"F47.wireOp",EDGE,"E59.left")])]});
            var sketch = newSketch(context, id + "F51", { "sketchPlane" : qUnion([Q0])});
            skLineSegment(sketch, "E62.bottom", {"start": v(-2500, 1117) * mm, "end": v(-2455, 1117) * mm});
            skLineSegment(sketch, "E62.top", {"start": v(-2500, 1072) * mm, "end": v(-2455, 1072) * mm});
            skLineSegment(sketch, "E62.left", {"start": v(-2500, 1117) * mm, "end": v(-2500, 1072) * mm});
            skLineSegment(sketch, "E62.right", {"start": v(-2455, 1117) * mm, "end": v(-2455, 1072) * mm});
            skSolve(sketch);
        }
        {
            var Q0;
            Q0 = qSketchRegion(id + "F51", true);
            extrude(context, id + "F52", {"entities" : qUnion([Q0]), "operationType" : NewBodyOperationType.ADD, "endBound" : BoundingType.UP_TO_NEXT, "depth" : 25 * mm, "offsetDistance" : 25 * mm});
        }
        {
            var Q0;
            Q0=makeQuery(id+"F52.boolean.opBoolean","MERGE",FACE,{"derivedFrom":[makeQuery(id+"F48.opExtrude","SWEPT_FACE",FACE,{"disambiguationData":[OSD([sQuery(id+"F47.wireOp",EDGE,"E59.bottom")])]}),makeQuery(id+"F48.opExtrude","SWEPT_FACE",FACE,{"disambiguationData":[OSD([sQuery(id+"F47.wireOp",EDGE,"E60.bottom")])]}),makeQuery(id+"F52.opExtrude","SWEPT_FACE",FACE,{"disambiguationData":[OSD([sQuery(id+"F51.wireOp",EDGE,"E62.right")])]})]});
            var sketch = newSketch(context, id + "F53", { "sketchPlane" : qUnion([Q0])});
            skLineSegment(sketch, "E63.bottom", {"start": v(750, 1117) * mm, "end": v(705, 1117) * mm});
            skLineSegment(sketch, "E63.top", {"start": v(750, 1072) * mm, "end": v(705, 1072) * mm});
            skLineSegment(sketch, "E63.left", {"start": v(750, 1117) * mm, "end": v(750, 1072) * mm});
            skLineSegment(sketch, "E63.right", {"start": v(705, 1117) * mm, "end": v(705, 1072) * mm});
            skLineSegment(sketch, "E64.bottom", {"start": v(-750, 1117) * mm, "end": v(-705, 1117) * mm});
            skLineSegment(sketch, "E64.top", {"start": v(-750, 1072) * mm, "end": v(-705, 1072) * mm});
            skLineSegment(sketch, "E64.left", {"start": v(-750, 1117) * mm, "end": v(-750, 1072) * mm});
            skLineSegment(sketch, "E64.right", {"start": v(-705, 1117) * mm, "end": v(-705, 1072) * mm});
            skSolve(sketch);
        }
        {
            var Q0;
            Q0 = qSketchRegion(id + "F53", true);
            extrude(context, id + "F54", {"entities" : qUnion([Q0]), "endBound" : BoundingType.UP_TO_NEXT, "depth" : 25 * mm, "offsetDistance" : 25 * mm});
        }
        {
            var Q0;
            Q0=makeQuery(id+"F1.opExtrude","SWEPT_BODY",BODY,{"disambiguationData":[OSD([sQuery(id+"F0.wireOp",EDGE,"E0.bottom"),sQuery(id+"F0.wireOp",EDGE,"E0.top"),sQuery(id+"F0.wireOp",EDGE,"E0.left"),sQuery(id+"F0.wireOp",EDGE,"E0.right"),sQuery(id+"F0.wireOp",EDGE,"E1.bottom"),sQuery(id+"F0.wireOp",EDGE,"E1.top"),sQuery(id+"F0.wireOp",EDGE,"E1.left"),sQuery(id+"F0.wireOp",EDGE,"E1.right")])]});
            var Q1;
            Q1=makeQuery(id+"F43.opExtrude","SWEPT_BODY",BODY,{"disambiguationData":[OSD([sQuery(id+"F42.wireOp",EDGE,"E48.bottom"),sQuery(id+"F42.wireOp",EDGE,"E48.top"),sQuery(id+"F42.wireOp",EDGE,"E48.left"),sQuery(id+"F42.wireOp",EDGE,"E48.right"),sQuery(id+"F42.wireOp",EDGE,"E49.bottom"),sQuery(id+"F42.wireOp",EDGE,"E49.top"),sQuery(id+"F42.wireOp",EDGE,"E49.left"),sQuery(id+"F42.wireOp",EDGE,"E49.right")])]});
            booleanBodies(context, id + "F55", {"operationType" : BooleanOperationType.SUBTRACTION, "tools" : qUnion([Q0]), "targets" : qUnion([Q1]), "keepTools" : true});
        }
        {
            var Q0;
            {var subQ0=makeQuery(id+"F3.opExtrude","SWEPT_FACE",FACE,{"disambiguationData":[OSD([sQuery(id+"F2.wireOp",EDGE,"E2.bottom")])]});var subQ1=sQuery(id+"F0.wireOp",EDGE,"E0.left");var subQ2=sQuery(id+"F0.wireOp",EDGE,"E1.right");var subQ3=sQuery(id+"F0.wireOp",EDGE,"E1.left");var subQ4=sQuery(id+"F0.wireOp",EDGE,"E1.top");var subQ5=sQuery(id+"F0.wireOp",EDGE,"E1.bottom");var subQ6=sQuery(id+"F0.wireOp",EDGE,"E0.right");var subQ7=sQuery(id+"F0.wireOp",EDGE,"E0.top");var subQ8=makeQuery(id+"F1.opExtrude","CAP_FACE",FACE,{"disambiguationData":[OSD([sQuery(id+"F0.wireOp",EDGE,"E0.bottom"),subQ7,subQ1,subQ6,subQ5,subQ4,subQ3,subQ2])],"isStart":false});var subQ9=makeQuery(id+"F39.opExtrude","SWEPT_FACE",FACE,{"disambiguationData":[OSD([sQuery(id+"F38.wireOp",EDGE,"E46.bottom")])]});var subQ10=makeQuery(id+"F3.opExtrude","SWEPT_FACE",FACE,{"disambiguationData":[OSD([sQuery(id+"F2.wireOp",EDGE,"E3.bottom")])]});Q0=makeQuery(id+"F48.boolean.opBoolean","SPLIT",FACE,{"disambiguationData":[TD([subQ8,makeQuery(id+"F1.opExtrude","SWEPT_FACE",FACE,{"disambiguationData":[OSD([subQ7])]}),makeQuery(id+"F1.opExtrude","SWEPT_FACE",FACE,{"disambiguationData":[OSD([subQ1])]}),makeQuery(id+"F1.opExtrude","SWEPT_FACE",FACE,{"disambiguationData":[OSD([subQ6])]}),makeQuery(id+"F1.opExtrude","SWEPT_FACE",FACE,{"disambiguationData":[OSD([subQ5])]}),makeQuery(id+"F1.opExtrude","SWEPT_FACE",FACE,{"disambiguationData":[OSD([subQ4])]}),makeQuery(id+"F1.opExtrude","SWEPT_FACE",FACE,{"disambiguationData":[OSD([subQ3])]}),makeQuery(id+"F1.opExtrude","SWEPT_FACE",FACE,{"disambiguationData":[OSD([subQ2])]}),subQ0,makeQuery(id+"F3.opExtrude","SWEPT_FACE",FACE,{"disambiguationData":[OSD([sQuery(id+"F2.wireOp",EDGE,"E2.left")])]}),subQ10,makeQuery(id+"F3.opExtrude","SWEPT_FACE",FACE,{"disambiguationData":[OSD([sQuery(id+"F2.wireOp",EDGE,"E3.left")])]}),subQ9,makeQuery(id+"F39.opExtrude","SWEPT_FACE",FACE,{"disambiguationData":[OSD([sQuery(id+"F38.wireOp",EDGE,"E46.left")])]}),makeQuery(id+"F39.opExtrude","SWEPT_FACE",FACE,{"disambiguationData":[OSD([sQuery(id+"F38.wireOp",EDGE,"E46.right")])]}),makeQuery(id+"F48.opExtrude","SWEPT_FACE",FACE,{"disambiguationData":[OSD([sQuery(id+"F47.wireOp",EDGE,"E59.bottom")])]}),makeQuery(id+"F48.opExtrude","SWEPT_FACE",FACE,{"disambiguationData":[OSD([sQuery(id+"F47.wireOp",EDGE,"E59.left")])]}),makeQuery(id+"F48.opExtrude","SWEPT_FACE",FACE,{"disambiguationData":[OSD([sQuery(id+"F47.wireOp",EDGE,"E59.right")])]}),makeQuery(id+"F48.opExtrude","SWEPT_FACE",FACE,{"disambiguationData":[OSD([sQuery(id+"F47.wireOp",EDGE,"E60.bottom")])]}),makeQuery(id+"F48.opExtrude","SWEPT_FACE",FACE,{"disambiguationData":[OSD([sQuery(id+"F47.wireOp",EDGE,"E60.left")])]}),makeQuery(id+"F48.opExtrude","SWEPT_FACE",FACE,{"disambiguationData":[OSD([sQuery(id+"F47.wireOp",EDGE,"E60.right")])]})])],"derivedFrom":makeQuery(id+"F39.boolean.opBoolean","MERGE",FACE,{"derivedFrom":[makeQuery(id+"F3.boolean.opBoolean","MERGE",FACE,{"derivedFrom":[subQ8,subQ0,subQ10]}),subQ9]})});}
            var sketch = newSketch(context, id + "F56", { "sketchPlane" : qUnion([Q0])});
            skLineSegment(sketch, "E65.bottom", {"start": v(-705, 1178) * mm, "end": v(-750, 1178) * mm});
            skLineSegment(sketch, "E65.top", {"start": v(-705, 1133) * mm, "end": v(-750, 1133) * mm});
            skLineSegment(sketch, "E65.left", {"start": v(-705, 1178) * mm, "end": v(-705, 1133) * mm});
            skLineSegment(sketch, "E65.right", {"start": v(-750, 1178) * mm, "end": v(-750, 1133) * mm});
            skLineSegment(sketch, "E66.bottom", {"start": v(-705, 333) * mm, "end": v(-750, 333) * mm});
            skLineSegment(sketch, "E66.top", {"start": v(-705, 288) * mm, "end": v(-750, 288) * mm});
            skLineSegment(sketch, "E66.left", {"start": v(-705, 333) * mm, "end": v(-705, 288) * mm});
            skLineSegment(sketch, "E66.right", {"start": v(-750, 333) * mm, "end": v(-750, 288) * mm});
            skSolve(sketch);
        }
        {
            var Q0;
            Q0 = qSketchRegion(id + "F56", true);
            extrude(context, id + "F57", {"entities" : qUnion([Q0]), "endBound" : BoundingType.UP_TO_NEXT, "depth" : 25 * mm, "offsetDistance" : 25 * mm});
        }
        {
            var Q0;
            Q0=makeQuery(id+"F55.opBoolean","MERGE",FACE,{"derivedFrom":[makeQuery(id+"F43.opExtrude","SWEPT_FACE",FACE,{"disambiguationData":[OSD([sQuery(id+"F42.wireOp",EDGE,"E48.left")])]})],"fromTools":[makeQuery(id+"F48.boolean.opBoolean","MERGE",FACE,{"derivedFrom":[makeQuery(id+"F3.boolean.opBoolean","MERGE",FACE,{"derivedFrom":[makeQuery(id+"F1.opExtrude","SWEPT_FACE",FACE,{"disambiguationData":[OSD([sQuery(id+"F0.wireOp",EDGE,"E0.left")])]}),makeQuery(id+"F3.opExtrude","SWEPT_FACE",FACE,{"disambiguationData":[OSD([sQuery(id+"F2.wireOp",EDGE,"E2.left")])]})]}),makeQuery(id+"F48.opExtrude","SWEPT_FACE",FACE,{"disambiguationData":[OSD([sQuery(id+"F47.wireOp",EDGE,"E60.right")])]})]})]});
            var sketch = newSketch(context, id + "F58", { "sketchPlane" : qUnion([Q0])});
            skLineSegment(sketch, "E67.bottom", {"start": v(-2500, 580.6) * mm, "end": v(-1700, 580.6) * mm});
            skLineSegment(sketch, "E67.top", {"start": v(-2500, 558.6) * mm, "end": v(-1700, 558.6) * mm});
            skLineSegment(sketch, "E67.left", {"start": v(-2500, 580.6) * mm, "end": v(-2500, 558.6) * mm});
            skLineSegment(sketch, "E67.right", {"start": v(-1700, 580.6) * mm, "end": v(-1700, 558.6) * mm});
            skLineSegment(sketch, "E68.bottom", {"start": v(-2111, 1117) * mm, "end": v(-2089, 1117) * mm});
            skLineSegment(sketch, "E68.top", {"start": v(-2111, 117) * mm, "end": v(-2089, 117) * mm});
            skLineSegment(sketch, "E68.left", {"start": v(-2111, 1117) * mm, "end": v(-2111, 117) * mm});
            skLineSegment(sketch, "E68.right", {"start": v(-2089, 1117) * mm, "end": v(-2089, 117) * mm});
            skLineSegment(sketch, "E69", {"start": v(-2100, 1104.47) * mm, "end": v(-2100, 909.13) * mm, "construction": true});
            skLineSegment(sketch, "E70.0", {"start": v(-2500, 52) * mm, "end": v(-2500, 1117) * mm, "construction": true});
            skLineSegment(sketch, "E71.0", {"start": v(-1700, 95) * mm, "end": v(-1700, 1117) * mm, "construction": true});
            skLineSegment(sketch, "E72", {"start": v(-2500, 569.6) * mm, "end": v(-2369.08, 569.6) * mm, "construction": true});
            skSolve(sketch);
        }
        {
            var Q0;
            Q0 = qSketchRegion(id + "F58", true);
            extrude(context, id + "F59", {"entities" : qUnion([Q0]), "depth" : 450 * mm, "offsetDistance" : 25 * mm});
        }
        {
            var Q0;
            Q0=makeQuery(id+"F43.opExtrude","SWEPT_FACE",FACE,{"disambiguationData":[OSD([sQuery(id+"F42.wireOp",EDGE,"E49.left")])]});
            var sketch = newSketch(context, id + "F60", { "sketchPlane" : qUnion([Q0])});
            skLineSegment(sketch, "E73.bottom", {"start": v(1728, 1067) * mm, "end": v(2472, 1067) * mm});
            skLineSegment(sketch, "E73.top", {"start": v(1728, 102) * mm, "end": v(2472, 102) * mm});
            skLineSegment(sketch, "E73.left", {"start": v(1728, 1067) * mm, "end": v(1728, 102) * mm});
            skLineSegment(sketch, "E73.right", {"start": v(2472, 1067) * mm, "end": v(2472, 102) * mm});
            skSolve(sketch);
        }
        {
            var Q0;
            Q0 = qSketchRegion(id + "F60", true);
            extrude(context, id + "F61", {"entities" : qUnion([Q0]), "operationType" : NewBodyOperationType.REMOVE, "oppositeDirection" : true, "depth" : 25 * mm, "offsetDistance" : 25 * mm});
        }
        {
            var Q0;
            Q0=makeQuery(id+"F43.opExtrude","SWEPT_FACE",FACE,{"disambiguationData":[OSD([sQuery(id+"F42.wireOp",EDGE,"E49.left")])]});
            var sketch = newSketch(context, id + "F62", { "sketchPlane" : qUnion([Q0])});
            skLineSegment(sketch, "E74.bottom", {"start": v(1708, 1087) * mm, "end": v(2492, 1087) * mm});
            skLineSegment(sketch, "E74.top", {"start": v(1708, 82) * mm, "end": v(2492, 82) * mm});
            skLineSegment(sketch, "E74.left", {"start": v(1708, 1087) * mm, "end": v(1708, 82) * mm});
            skLineSegment(sketch, "E74.right", {"start": v(2492, 1087) * mm, "end": v(2492, 82) * mm});
            skSolve(sketch);
        }
        {
            var Q0;
            Q0 = qSketchRegion(id + "F62", true);
            extrude(context, id + "F63", {"entities" : qUnion([Q0]), "depth" : 22 * mm, "offsetDistance" : 25 * mm});
        }
        {
            var Q0;
            Q0=makeQuery(id+"F43.opExtrude","SWEPT_FACE",FACE,{"disambiguationData":[OSD([sQuery(id+"F42.wireOp",EDGE,"E49.bottom")])]});
            var sketch = newSketch(context, id + "F64", { "sketchPlane" : qUnion([Q0])});
            skLineSegment(sketch, "E75.bottom", {"start": v(-692, 1037) * mm, "end": v(-252, 1037) * mm});
            skLineSegment(sketch, "E75.top", {"start": v(-692, 75) * mm, "end": v(-252, 75) * mm});
            skLineSegment(sketch, "E75.left", {"start": v(-692, 1037) * mm, "end": v(-692, 75) * mm});
            skLineSegment(sketch, "E75.right", {"start": v(-252, 1037) * mm, "end": v(-252, 75) * mm});
            skSolve(sketch);
        }
        {
            var Q0;
            Q0 = qSketchRegion(id + "F64", true);
            extrude(context, id + "F65", {"entities" : qUnion([Q0]), "depth" : 22 * mm, "offsetDistance" : 25 * mm});
        }
        {
            var Q0;
            Q0=makeQuery(id+"F43.opExtrude","SWEPT_FACE",FACE,{"disambiguationData":[OSD([sQuery(id+"F42.wireOp",EDGE,"E49.left")])]});
            var sketch = newSketch(context, id + "F66", { "sketchPlane" : qUnion([Q0])});
            skLineSegment(sketch, "E76", {"start": v(1678, 1117) * mm, "end": v(2089, 1317) * mm});
            skLineSegment(sketch, "E77", {"start": v(2089, 1317) * mm, "end": v(2522, 1117) * mm});
            skLineSegment(sketch, "E78", {"start": v(2522, 1117) * mm, "end": v(1678, 1117) * mm});
            skSolve(sketch);
        }
        {
            var Q0;
            Q0 = qSketchRegion(id + "F66", true);
            var Q1;
            Q1=makeQuery(id+"F43.opExtrude","SWEPT_FACE",FACE,{"disambiguationData":[OSD([sQuery(id+"F42.wireOp",EDGE,"E49.right")])]});
            extrude(context, id + "F67", {"entities" : qUnion([Q0]), "endBound" : BoundingType.UP_TO_SURFACE, "oppositeDirection" : true, "depth" : 25 * mm, "endBoundEntityFace" : qUnion([Q1]), "offsetDistance" : 25 * mm});
        }
        {
            var Q0;
            {var subQ0=makeQuery(id+"F48.boolean.opBoolean","MERGE",FACE,{"derivedFrom":[makeQuery(id+"F3.boolean.opBoolean","MERGE",FACE,{"derivedFrom":[makeQuery(id+"F1.opExtrude","SWEPT_FACE",FACE,{"disambiguationData":[OSD([sQuery(id+"F0.wireOp",EDGE,"E0.right")])]}),makeQuery(id+"F3.opExtrude","SWEPT_FACE",FACE,{"disambiguationData":[OSD([sQuery(id+"F2.wireOp",EDGE,"E3.left")])]})]}),makeQuery(id+"F48.opExtrude","SWEPT_FACE",FACE,{"disambiguationData":[OSD([sQuery(id+"F47.wireOp",EDGE,"E59.right")])]})]});Q0=qUnion([subQ0,makeQuery(id+"F55.opBoolean","MERGE",FACE,{"derivedFrom":[makeQuery(id+"F43.opExtrude","SWEPT_FACE",FACE,{"disambiguationData":[OSD([sQuery(id+"F42.wireOp",EDGE,"E48.right")])]})],"fromTools":[subQ0]})]);}
            var sketch = newSketch(context, id + "F68", { "sketchPlane" : qUnion([Q0])});
            skLineSegment(sketch, "E79.bottom", {"start": v(1061, 1072) * mm, "end": v(1106, 1072) * mm});
            skLineSegment(sketch, "E79.top", {"start": v(1061, 95) * mm, "end": v(1106, 95) * mm});
            skLineSegment(sketch, "E79.left", {"start": v(1061, 1072) * mm, "end": v(1061, 95) * mm});
            skLineSegment(sketch, "E79.right", {"start": v(1106, 1072) * mm, "end": v(1106, 95) * mm});
            skLineSegment(sketch, "E80", {"start": v(-288, 921.49) * mm, "end": v(1061, 921.49) * mm, "construction": true});
            skLineSegment(sketch, "E81", {"start": v(1106, 429.1) * mm, "end": v(2455, 429.1) * mm, "construction": true});
            skLineSegment(sketch, "E82", {"start": v(-288, 1072) * mm, "end": v(1061, 95) * mm});
            skLineSegment(sketch, "E83", {"start": v(1061, 150.56) * mm, "end": v(-211.28, 1072) * mm});
            skLineSegment(sketch, "E84", {"start": v(-211.28, 1072) * mm, "end": v(-288, 1072) * mm});
            skLineSegment(sketch, "E85", {"start": v(1106, 95) * mm, "end": v(2455, 1072) * mm});
            skLineSegment(sketch, "E86", {"start": v(2455, 1072) * mm, "end": v(2378.28, 1072) * mm});
            skLineSegment(sketch, "E87", {"start": v(2378.28, 1072) * mm, "end": v(1106, 150.56) * mm});
            skLineSegment(sketch, "E88", {"start": v(1106, 150.56) * mm, "end": v(1106, 95) * mm});
            skSolve(sketch);
        }
        {
            var Q0;
            Q0 = qSketchRegion(id + "F68", true);
            extrude(context, id + "F69", {"entities" : qUnion([Q0]), "oppositeDirection" : true, "depth" : 45 * mm, "offsetDistance" : 25 * mm});
        }
        {
            var Q0;
            Q0=makeQuery(id+"F1.opExtrude","SWEPT_FACE",FACE,{"disambiguationData":[OSD([sQuery(id+"F0.wireOp",EDGE,"E0.bottom")])]});
            var sketch = newSketch(context, id + "F70", { "sketchPlane" : qUnion([Q0])});
            skLineSegment(sketch, "E89", {"start": v(-705, 95) * mm, "end": v(705, 1072) * mm});
            skLineSegment(sketch, "E90", {"start": v(705, 1072) * mm, "end": v(625.99, 1072) * mm});
            skLineSegment(sketch, "E91", {"start": v(625.99, 1072) * mm, "end": v(-705, 149.75) * mm});
            skLineSegment(sketch, "E92", {"start": v(-705, 149.75) * mm, "end": v(-705, 95) * mm});
            skSolve(sketch);
        }
        {
            var Q0;
            Q0 = qSketchRegion(id + "F70", true);
            extrude(context, id + "F71", {"entities" : qUnion([Q0]), "oppositeDirection" : true, "depth" : 45 * mm, "offsetDistance" : 25 * mm});
        }
        {
            var Q0;
            {var subQ0=makeQuery(id+"F48.boolean.opBoolean","MERGE",FACE,{"derivedFrom":[makeQuery(id+"F3.boolean.opBoolean","MERGE",FACE,{"derivedFrom":[makeQuery(id+"F1.opExtrude","SWEPT_FACE",FACE,{"disambiguationData":[OSD([sQuery(id+"F0.wireOp",EDGE,"E0.left")])]}),makeQuery(id+"F3.opExtrude","SWEPT_FACE",FACE,{"disambiguationData":[OSD([sQuery(id+"F2.wireOp",EDGE,"E2.left")])]})]}),makeQuery(id+"F48.opExtrude","SWEPT_FACE",FACE,{"disambiguationData":[OSD([sQuery(id+"F47.wireOp",EDGE,"E60.right")])]})]});Q0=qUnion([subQ0,makeQuery(id+"F55.opBoolean","MERGE",FACE,{"derivedFrom":[makeQuery(id+"F43.opExtrude","SWEPT_FACE",FACE,{"disambiguationData":[OSD([sQuery(id+"F42.wireOp",EDGE,"E48.left")])]})],"fromTools":[subQ0]})]);}
            var sketch = newSketch(context, id + "F72", { "sketchPlane" : qUnion([Q0])});
            skLineSegment(sketch, "E93.bottom", {"start": v(-411, 95) * mm, "end": v(-366, 95) * mm});
            skLineSegment(sketch, "E93.top", {"start": v(-411, 1072) * mm, "end": v(-366, 1072) * mm});
            skLineSegment(sketch, "E93.left", {"start": v(-411, 95) * mm, "end": v(-411, 1072) * mm});
            skLineSegment(sketch, "E93.right", {"start": v(-366, 95) * mm, "end": v(-366, 1072) * mm});
            skLineSegment(sketch, "E94", {"start": v(-411, 784.23) * mm, "end": v(-2455, 784.23) * mm, "construction": true});
            skLineSegment(sketch, "E95", {"start": v(-366, 441.84) * mm, "end": v(1678, 441.84) * mm, "construction": true});
            skLineSegment(sketch, "E96", {"start": v(-411, 1072) * mm, "end": v(-2455, 95) * mm});
            skLineSegment(sketch, "E97", {"start": v(-2455, 95) * mm, "end": v(-2350.65, 95) * mm});
            skLineSegment(sketch, "E98", {"start": v(-2350.65, 95) * mm, "end": v(-411, 1022.12) * mm});
            skLineSegment(sketch, "E99", {"start": v(-411, 1022.12) * mm, "end": v(-411, 1072) * mm});
            skLineSegment(sketch, "E100", {"start": v(-366, 1072) * mm, "end": v(1678, 95) * mm});
            skLineSegment(sketch, "E101", {"start": v(1678, 95) * mm, "end": v(1573.65, 95) * mm});
            skLineSegment(sketch, "E102", {"start": v(1573.65, 95) * mm, "end": v(-366, 1022.12) * mm});
            skLineSegment(sketch, "E103", {"start": v(-366, 1022.12) * mm, "end": v(-366, 1072) * mm});
            skSolve(sketch);
        }
        {
            var Q0;
            Q0 = qSketchRegion(id + "F72", true);
            extrude(context, id + "F73", {"entities" : qUnion([Q0]), "oppositeDirection" : true, "depth" : 45 * mm, "offsetDistance" : 25 * mm});
        }
        {
            var Q0;
            Q0=makeQuery(id+"F54.opExtrude","SWEPT_FACE",FACE,{"disambiguationData":[OSD([sQuery(id+"F53.wireOp",EDGE,"E63.bottom")])]});
            var sketch = newSketch(context, id + "F74", { "sketchPlane" : qUnion([Q0])});
            skLineSegment(sketch, "E104", {"start": v(-705, 1678) * mm, "end": v(705, -310.7) * mm});
            skLineSegment(sketch, "E105", {"start": v(705, -310.7) * mm, "end": v(705, -466.3) * mm});
            skLineSegment(sketch, "E106", {"start": v(705, -466.3) * mm, "end": v(-705, -2455) * mm});
            skLineSegment(sketch, "E107", {"start": v(-705, -2455) * mm, "end": v(-705, -2377.2) * mm});
            skLineSegment(sketch, "E108", {"start": v(-705, -2377.2) * mm, "end": v(705, -388.5) * mm});
            skLineSegment(sketch, "E109", {"start": v(705, -388.5) * mm, "end": v(-705, 1600.2) * mm});
            skLineSegment(sketch, "E110", {"start": v(-705, 1600.2) * mm, "end": v(-705, 1678) * mm});
            skLineSegment(sketch, "E111", {"start": v(325.83, -388.5) * mm, "end": v(1714.17, -388.5) * mm, "construction": true});
            skSolve(sketch);
        }
        {
            var Q0;
            Q0 = qSketchRegion(id + "F74", true);
            extrude(context, id + "F75", {"entities" : qUnion([Q0]), "oppositeDirection" : true, "depth" : 45 * mm, "offsetDistance" : 25 * mm});
        }
    });
